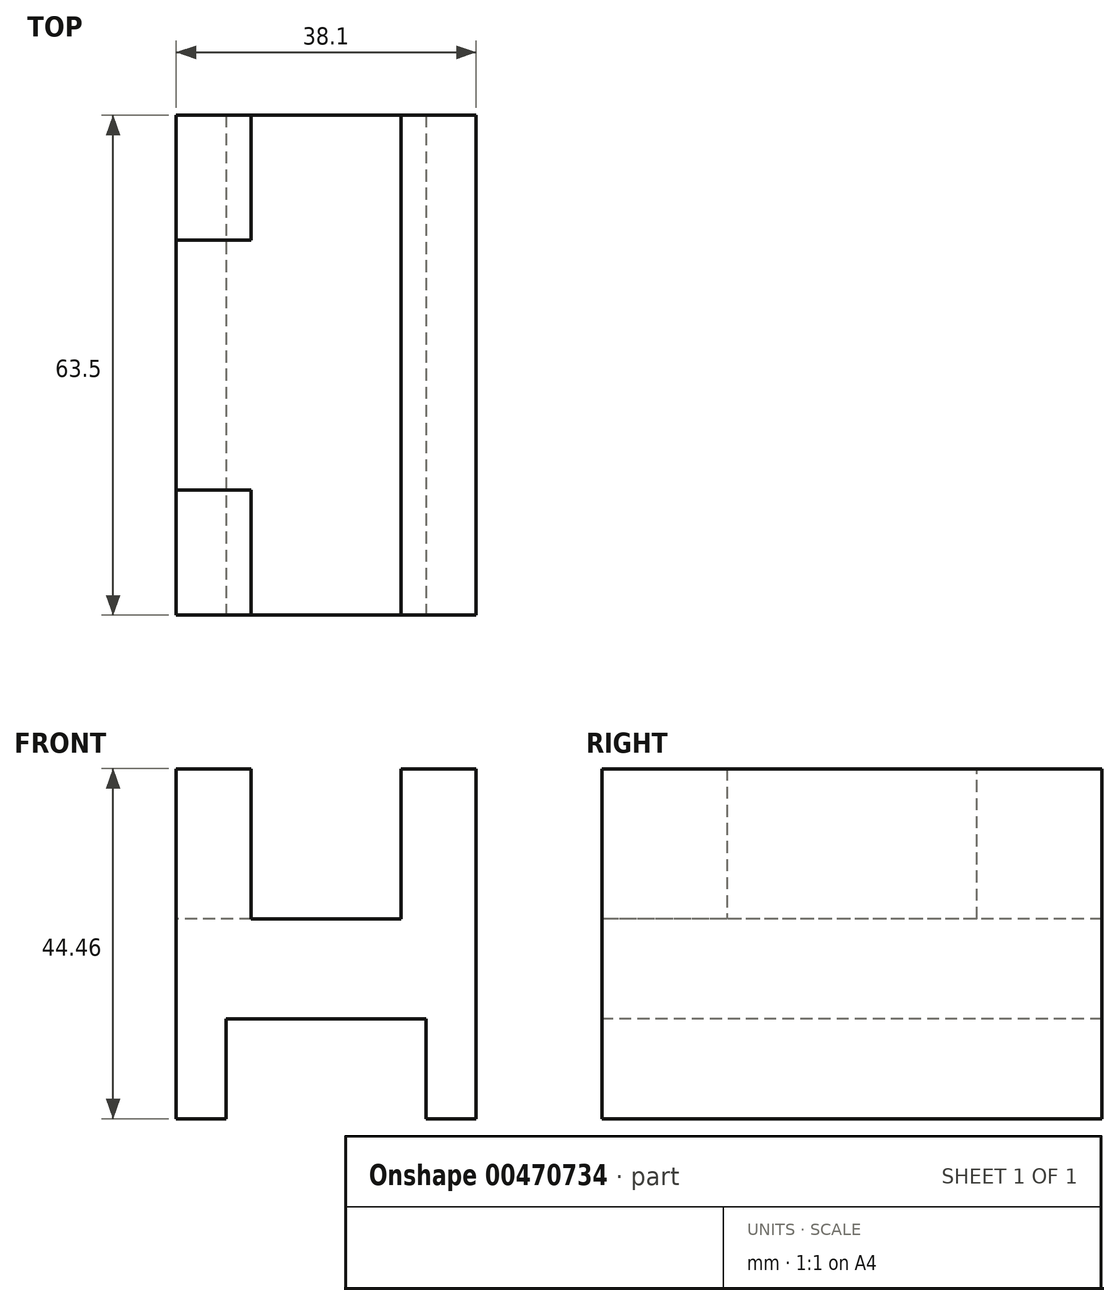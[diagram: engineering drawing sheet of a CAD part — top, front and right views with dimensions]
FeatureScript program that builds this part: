
annotation { "Feature Type Name" : "Feature", "Feature Type Description" : "" }
export const myFeature = defineFeature(function(context is Context, id is Id, definition is map)
    precondition{}
    {
        {
            var Q0;
            Q0=qCreatedBy(makeId("Front.planeOp"),FACE);
            var sketch = newSketch(context, id + "F0", { "sketchPlane" : qUnion([Q0])});
            skLineSegment(sketch, "E0.bottom", {"start": v(-19.05, 22.23) * mm, "end": v(19.05, 22.23) * mm});
            skLineSegment(sketch, "E0.top", {"start": v(-19.05, -22.23) * mm, "end": v(19.05, -22.23) * mm});
            skLineSegment(sketch, "E0.left", {"start": v(-19.05, 22.23) * mm, "end": v(-19.05, -22.22) * mm});
            skLineSegment(sketch, "E0.right", {"start": v(19.05, 22.23) * mm, "end": v(19.05, -22.22) * mm});
            skPoint(sketch, "E0.middle", {"position": v(0, 0) * mm});
            skSolve(sketch);
        }
        {
            var Q0;
            Q0 = qSketchRegion(id + "F0", true);
            extrude(context, id + "F1", {"entities" : qUnion([Q0]), "depth" : 63.5 * mm});
        }
        {
            var Q0;
            Q0=makeQuery(id+"F1.opExtrude","CAP_FACE",FACE,{"disambiguationData":[OSD([sQuery(id+"F0.wireOp",EDGE,"E0.bottom"),sQuery(id+"F0.wireOp",EDGE,"E0.top"),sQuery(id+"F0.wireOp",EDGE,"E0.left"),sQuery(id+"F0.wireOp",EDGE,"E0.right")])],"isStart":false});
            var sketch = newSketch(context, id + "F2", { "sketchPlane" : qUnion([Q0])});
            skLineSegment(sketch, "E1.bottom", {"start": v(-9.53, 22.23) * mm, "end": v(9.53, 22.23) * mm});
            skLineSegment(sketch, "E1.top", {"start": v(-9.52, 3.18) * mm, "end": v(9.53, 3.18) * mm});
            skLineSegment(sketch, "E1.left", {"start": v(-9.52, 22.23) * mm, "end": v(-9.52, 3.18) * mm});
            skLineSegment(sketch, "E1.right", {"start": v(9.53, 22.23) * mm, "end": v(9.53, 3.18) * mm});
            skSolve(sketch);
        }
        {
            var Q0;
            Q0 = qSketchRegion(id + "F2", true);
            extrude(context, id + "F3", {"entities" : qUnion([Q0]), "operationType" : NewBodyOperationType.REMOVE, "endBound" : BoundingType.THROUGH_ALL, "oppositeDirection" : true, "depth" : 25.4 * mm});
        }
        {
            var Q0;
            Q0=makeQuery(id+"F1.opExtrude","CAP_FACE",FACE,{"disambiguationData":[OSD([sQuery(id+"F0.wireOp",EDGE,"E0.bottom"),sQuery(id+"F0.wireOp",EDGE,"E0.top"),sQuery(id+"F0.wireOp",EDGE,"E0.left"),sQuery(id+"F0.wireOp",EDGE,"E0.right")])],"isStart":false});
            var sketch = newSketch(context, id + "F4", { "sketchPlane" : qUnion([Q0])});
            skLineSegment(sketch, "E2.bottom", {"start": v(-12.7, -9.52) * mm, "end": v(12.7, -9.52) * mm});
            skLineSegment(sketch, "E2.top", {"start": v(-12.7, -22.23) * mm, "end": v(12.7, -22.23) * mm});
            skLineSegment(sketch, "E2.left", {"start": v(-12.7, -9.53) * mm, "end": v(-12.7, -22.23) * mm});
            skLineSegment(sketch, "E2.right", {"start": v(12.7, -9.53) * mm, "end": v(12.7, -22.23) * mm});
            skSolve(sketch);
        }
        {
            var Q0;
            Q0 = qSketchRegion(id + "F4", true);
            extrude(context, id + "F5", {"entities" : qUnion([Q0]), "operationType" : NewBodyOperationType.REMOVE, "endBound" : BoundingType.THROUGH_ALL, "oppositeDirection" : true, "depth" : 25.4 * mm});
        }
        {
            var Q0;
            Q0=makeQuery(id+"F1.opExtrude","SWEPT_FACE",FACE,{"disambiguationData":[OSD([sQuery(id+"F0.wireOp",EDGE,"E0.left")])]});
            var sketch = newSketch(context, id + "F6", { "sketchPlane" : qUnion([Q0])});
            skLineSegment(sketch, "E3.bottom", {"start": v(15.88, 22.22) * mm, "end": v(47.62, 22.22) * mm});
            skLineSegment(sketch, "E3.top", {"start": v(15.88, 3.17) * mm, "end": v(47.62, 3.17) * mm});
            skLineSegment(sketch, "E3.left", {"start": v(15.88, 22.22) * mm, "end": v(15.88, 3.17) * mm});
            skLineSegment(sketch, "E3.right", {"start": v(47.62, 22.22) * mm, "end": v(47.62, 3.17) * mm});
            skSolve(sketch);
        }
        {
            var Q0;
            Q0 = qSketchRegion(id + "F6", true);
            extrude(context, id + "F7", {"entities" : qUnion([Q0]), "operationType" : NewBodyOperationType.REMOVE, "endBound" : BoundingType.UP_TO_NEXT, "oppositeDirection" : true, "depth" : 25.4 * mm});
        }
    });
